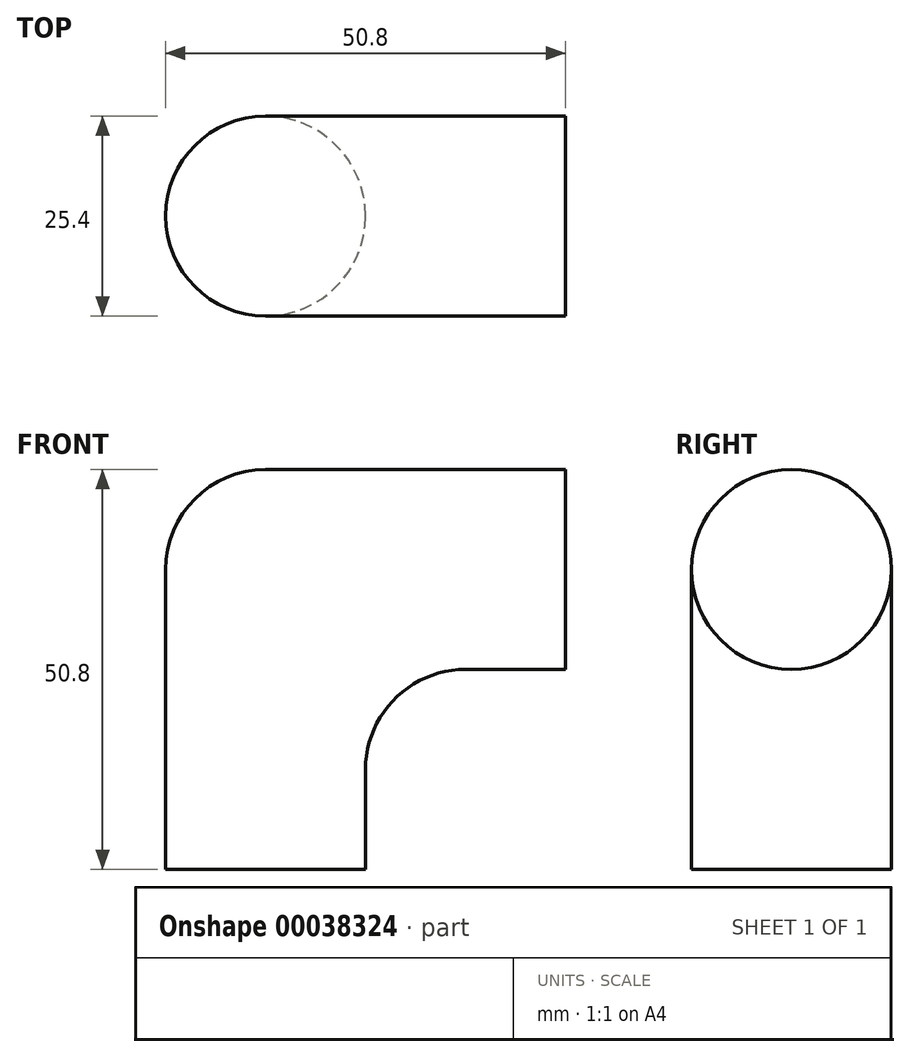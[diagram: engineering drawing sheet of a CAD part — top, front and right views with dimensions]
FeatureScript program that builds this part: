
annotation { "Feature Type Name" : "Feature", "Feature Type Description" : "" }
export const myFeature = defineFeature(function(context is Context, id is Id, definition is map)
    precondition{}
    {
        {
            var Q0;
            Q0=qCreatedBy(makeId("Front.planeOp"),FACE);
            var sketch = newSketch(context, id + "F0", { "sketchPlane" : qUnion([Q0])});
            skLineSegment(sketch, "E0.bottom", {"start": v(-56.34, 41.37) * mm, "end": v(-30.94, 41.37) * mm});
            skLineSegment(sketch, "E0.top", {"start": v(-56.34, -9.43) * mm, "end": v(-30.94, -9.43) * mm});
            skLineSegment(sketch, "E0.left", {"start": v(-56.34, 41.37) * mm, "end": v(-56.34, -9.43) * mm});
            skLineSegment(sketch, "E0.right", {"start": v(-30.94, 41.37) * mm, "end": v(-30.94, -9.43) * mm});
            skLineSegment(sketch, "E1.bottom", {"start": v(-30.94, 41.37) * mm, "end": v(-5.54, 41.37) * mm});
            skLineSegment(sketch, "E1.top", {"start": v(-30.94, 15.97) * mm, "end": v(-5.54, 15.97) * mm});
            skLineSegment(sketch, "E1.left", {"start": v(-30.94, 41.37) * mm, "end": v(-30.94, 15.97) * mm});
            skLineSegment(sketch, "E1.right", {"start": v(-5.54, 41.37) * mm, "end": v(-5.54, 15.97) * mm});
            skSolve(sketch);
        }
        {
            var Q0;
            Q0=makeQuery(id+"F0.imprint","IMPRINT",FACE,{"disambiguationData":[TD([[makeQuery(id+"F0.imprint","IMPRINT",EDGE,{"derivedFrom":sQuery(id+"F0.wireOp",EDGE,"E0.bottom")}),-1.0]])]});
            var Q1;
            Q1=makeQuery(id+"F0.imprint","IMPRINT",FACE,{"disambiguationData":[TD([[makeQuery(id+"F0.imprint","IMPRINT",EDGE,{"derivedFrom":sQuery(id+"F0.wireOp",EDGE,"E1.bottom")}),-1.0]])]});
            extrude(context, id + "F1", {"entities" : qUnion([Q0, Q1]), "depth" : 25.4 * mm});
        }
        {
            var Q0;
            Q0=makeQuery(id+"F1.opExtrude","CAP_EDGE",EDGE,{"disambiguationData":[OSD([sQuery(id+"F0.wireOp",EDGE,"E0.left")])],"isStart":true});
            var Q1;
            Q1=makeQuery(id+"F1.opExtrude","CAP_EDGE",EDGE,{"disambiguationData":[OSD([sQuery(id+"F0.wireOp",EDGE,"E0.left")])],"isStart":false});
            var Q2;
            Q2=makeQuery(id+"F1.opExtrude","CAP_EDGE",EDGE,{"disambiguationData":[OSD([sQuery(id+"F0.wireOp",EDGE,"E0.bottom"),sQuery(id+"F0.wireOp",EDGE,"E1.bottom")])],"isStart":false});
            var Q3;
            Q3=makeQuery(id+"F1.opExtrude","SWEPT_EDGE",EDGE,{"disambiguationData":[OSD([sQuery(id+"F0.wireOp",EDGE,"E0.bottom"),sQuery(id+"F0.wireOp",EDGE,"E0.left")])]});
            var Q4;
            Q4=makeQuery(id+"F1.opExtrude","CAP_EDGE",EDGE,{"disambiguationData":[OSD([sQuery(id+"F0.wireOp",EDGE,"E0.bottom"),sQuery(id+"F0.wireOp",EDGE,"E1.bottom")])],"isStart":true});
            var Q5;
            Q5=makeQuery(id+"F1.opExtrude","CAP_EDGE",EDGE,{"disambiguationData":[OSD([sQuery(id+"F0.wireOp",EDGE,"E1.top")])],"isStart":false});
            var Q6;
            Q6=makeQuery(id+"F1.opExtrude","CAP_EDGE",EDGE,{"disambiguationData":[OSD([sQuery(id+"F0.wireOp",EDGE,"E0.right")])],"isStart":false});
            var Q7;
            Q7=makeQuery(id+"F1.opExtrude","CAP_EDGE",EDGE,{"disambiguationData":[OSD([sQuery(id+"F0.wireOp",EDGE,"E0.right")])],"isStart":true});
            var Q8;
            Q8=makeQuery(id+"F1.opExtrude","CAP_EDGE",EDGE,{"disambiguationData":[OSD([sQuery(id+"F0.wireOp",EDGE,"E1.top")])],"isStart":true});
            var Q9;
            Q9=makeQuery(id+"F1.opExtrude","SWEPT_EDGE",EDGE,{"disambiguationData":[OSD([sQuery(id+"F0.wireOp",EDGE,"E0.right"),sQuery(id+"F0.wireOp",EDGE,"E1.top"),sQuery(id+"F0.wireOp",EDGE,"E1.left")])]});
            fillet(context, id + "F2", {"entities" : qUnion([Q0, Q1, Q2, Q3, Q4, Q5, Q6, Q7, Q8, Q9]), "radius" : 12.7 * mm, "tangentPropagation" : true, "allowEdgeOverflow" : false});
        }
    });
